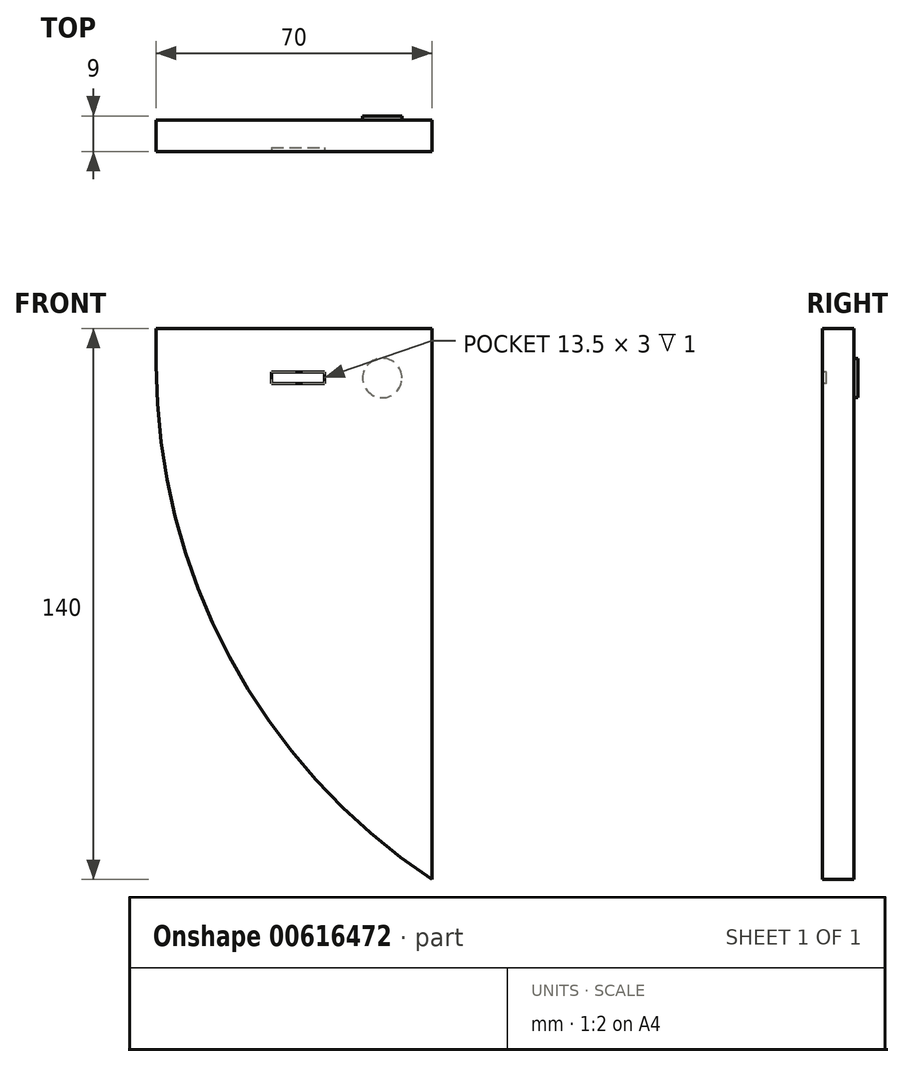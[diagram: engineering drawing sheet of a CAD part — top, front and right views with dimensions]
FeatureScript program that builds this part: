
annotation { "Feature Type Name" : "Feature", "Feature Type Description" : "" }
export const myFeature = defineFeature(function(context is Context, id is Id, definition is map)
    precondition{}
    {
        {
            var Q0;
            Q0=qCreatedBy(makeId("Front.planeOp"),FACE);
            var sketch = newSketch(context, id + "F0", { "sketchPlane" : qUnion([Q0])});
            skLineSegment(sketch, "E0.bottom", {"start": v(-29.27, 89.69) * mm, "end": v(40.73, 89.69) * mm});
            skLineSegment(sketch, "E0.top", {"start": v(-29.27, -50.31) * mm, "end": v(40.73, -50.31) * mm});
            skLineSegment(sketch, "E0.left", {"start": v(-29.27, 89.69) * mm, "end": v(-29.27, -50.31) * mm});
            skLineSegment(sketch, "E0.right", {"start": v(40.73, 89.69) * mm, "end": v(40.73, -50.31) * mm});
            skSolve(sketch);
        }
        {
            var Q0;
            Q0 = qSketchRegion(id + "F0", true);
            extrude(context, id + "F1", {"entities" : qUnion([Q0]), "depth" : 8 * mm, "offsetDistance" : 25 * mm});
        }
        {
            var Q0;
            Q0=makeQuery(id+"F1.opExtrude","CAP_FACE",FACE,{"disambiguationData":[OSD([sQuery(id+"F0.wireOp",EDGE,"E0.bottom"),sQuery(id+"F0.wireOp",EDGE,"E0.top"),sQuery(id+"F0.wireOp",EDGE,"E0.left"),sQuery(id+"F0.wireOp",EDGE,"E0.right")])],"isStart":false});
            var sketch = newSketch(context, id + "F2", { "sketchPlane" : qUnion([Q0])});
            skLineSegment(sketch, "E1.bottom", {"start": v(0, 75.69) * mm, "end": v(13.5, 75.69) * mm});
            skLineSegment(sketch, "E1.top", {"start": v(0, 78.69) * mm, "end": v(13.5, 78.69) * mm});
            skLineSegment(sketch, "E1.left", {"start": v(0, 75.69) * mm, "end": v(0, 78.69) * mm});
            skLineSegment(sketch, "E1.right", {"start": v(13.5, 75.69) * mm, "end": v(13.5, 78.69) * mm});
            skSolve(sketch);
        }
        {
            var Q0;
            Q0 = qSketchRegion(id + "F2", true);
            extrude(context, id + "F3", {"entities" : qUnion([Q0]), "operationType" : NewBodyOperationType.REMOVE, "oppositeDirection" : true, "depth" : 1 * mm, "offsetDistance" : 25 * mm});
        }
        {
            var Q0;
            Q0=makeQuery(id+"F1.opExtrude","CAP_FACE",FACE,{"disambiguationData":[OSD([sQuery(id+"F0.wireOp",EDGE,"E0.bottom"),sQuery(id+"F0.wireOp",EDGE,"E0.top"),sQuery(id+"F0.wireOp",EDGE,"E0.left"),sQuery(id+"F0.wireOp",EDGE,"E0.right")])],"isStart":false});
            var sketch = newSketch(context, id + "F4", { "sketchPlane" : qUnion([Q0])});
            skCircle(sketch, "E2", {"center": v(6.84, -41.06) * mm, "radius": 2.25 * mm});
            skSolve(sketch);
        }
        {
            var Q0;
            Q0 = qSketchRegion(id + "F4", true);
            extrude(context, id + "F5", {"entities" : qUnion([Q0]), "operationType" : NewBodyOperationType.REMOVE, "oppositeDirection" : true, "depth" : 0.5 * mm, "offsetDistance" : 25 * mm});
        }
        {
            var Q0;
            Q0=makeQuery(id+"F1.opExtrude","CAP_FACE",FACE,{"disambiguationData":[OSD([sQuery(id+"F0.wireOp",EDGE,"E0.bottom"),sQuery(id+"F0.wireOp",EDGE,"E0.top"),sQuery(id+"F0.wireOp",EDGE,"E0.left"),sQuery(id+"F0.wireOp",EDGE,"E0.right")])],"isStart":true});
            var sketch = newSketch(context, id + "F6", { "sketchPlane" : qUnion([Q0])});
            skCircle(sketch, "E3", {"center": v(-28.15, 77.1) * mm, "radius": 5 * mm});
            skSolve(sketch);
        }
        {
            var Q0;
            Q0 = qSketchRegion(id + "F6", true);
            extrude(context, id + "F7", {"entities" : qUnion([Q0]), "operationType" : NewBodyOperationType.ADD, "depth" : 1 * mm, "offsetDistance" : 25 * mm});
        }
        {
            var Q0;
            Q0=makeQuery(id+"FVfXy9b7Kb0hSOM_1.opFillet","BLEND_EDGE",EDGE,{"blendedFrom":[makeQuery(id+"F1.opExtrude","CAP_EDGE",EDGE,{"disambiguationData":[OSD([sQuery(id+"F0.wireOp",EDGE,"E0.bottom")])],"isStart":false}),makeQuery(id+"F1.opExtrude","CAP_EDGE",EDGE,{"disambiguationData":[OSD([sQuery(id+"F0.wireOp",EDGE,"E0.left")])],"isStart":false})],"blendedInto":[]});
            var Q1;
            Q1=makeQuery(id+"FVfXy9b7Kb0hSOM_1.opFillet","BLEND_EDGE",EDGE,{"blendedFrom":[makeQuery(id+"F1.opExtrude","CAP_EDGE",EDGE,{"disambiguationData":[OSD([sQuery(id+"F0.wireOp",EDGE,"E0.bottom")])],"isStart":false}),makeQuery(id+"F1.opExtrude","CAP_EDGE",EDGE,{"disambiguationData":[OSD([sQuery(id+"F0.wireOp",EDGE,"E0.right")])],"isStart":false})],"blendedInto":[]});
            var Q2;
            Q2=makeQuery(id+"FVfXy9b7Kb0hSOM_1.opFillet","BLEND_EDGE",EDGE,{"blendedFrom":[makeQuery(id+"F1.opExtrude","CAP_EDGE",EDGE,{"disambiguationData":[OSD([sQuery(id+"F0.wireOp",EDGE,"E0.top")])],"isStart":false}),makeQuery(id+"F1.opExtrude","CAP_EDGE",EDGE,{"disambiguationData":[OSD([sQuery(id+"F0.wireOp",EDGE,"E0.right")])],"isStart":false})],"blendedInto":[]});
            var Q3;
            Q3=makeQuery(id+"FVfXy9b7Kb0hSOM_1.opFillet","BLEND_EDGE",EDGE,{"blendedFrom":[makeQuery(id+"F1.opExtrude","CAP_EDGE",EDGE,{"disambiguationData":[OSD([sQuery(id+"F0.wireOp",EDGE,"E0.top")])],"isStart":false}),makeQuery(id+"F1.opExtrude","CAP_EDGE",EDGE,{"disambiguationData":[OSD([sQuery(id+"F0.wireOp",EDGE,"E0.left")])],"isStart":false})],"blendedInto":[]});
            var Q4;
            Q4=makeQuery(id+"F1.opExtrude","SWEPT_EDGE",EDGE,{"disambiguationData":[OSD([sQuery(id+"F0.wireOp",EDGE,"E0.top"),sQuery(id+"F0.wireOp",EDGE,"E0.left")])]});
            fillet(context, id + "F8", {"entities" : qUnion([Q0, Q1, Q2, Q3, Q4]), "radius" : 157.06 * mm, "tangentPropagation" : true, "allowEdgeOverflow" : false});
        }
    });
